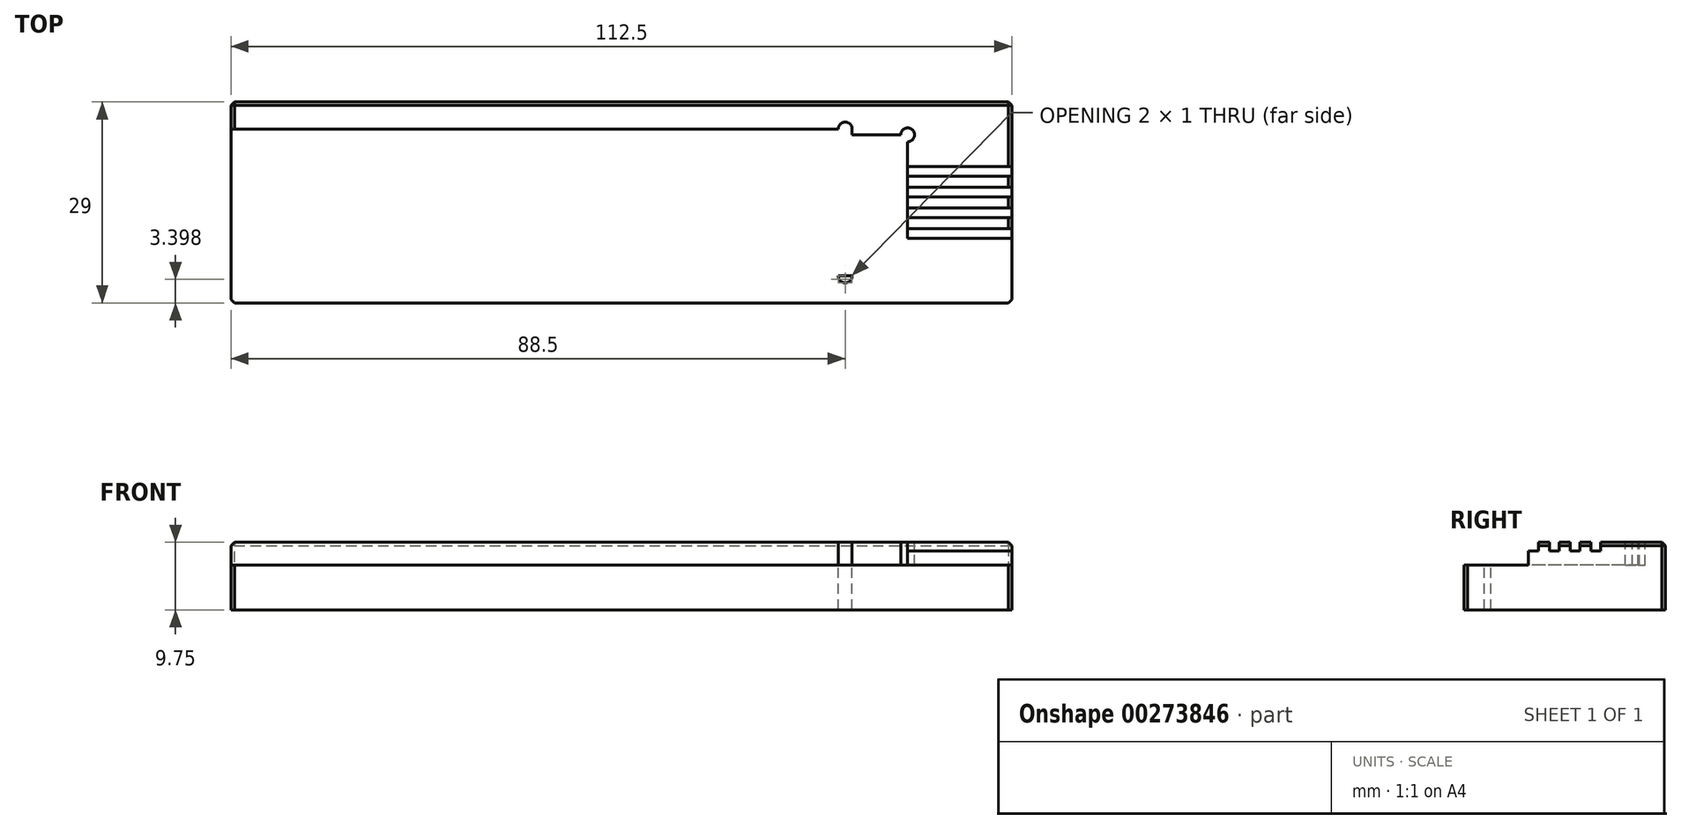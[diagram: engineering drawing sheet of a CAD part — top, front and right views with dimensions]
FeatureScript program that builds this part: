
annotation { "Feature Type Name" : "Feature", "Feature Type Description" : "" }
export const myFeature = defineFeature(function(context is Context, id is Id, definition is map)
    precondition{}
    {
        {
            var Q0;
            Q0=qCreatedBy(makeId("Top.planeOp"),FACE);
            var sketch = newSketch(context, id + "F0", { "sketchPlane" : qUnion([Q0])});
            skLineSegment(sketch, "E0.bottom", {"start": v(-42.98, 19.05) * mm, "end": v(69.52, 19.05) * mm});
            skLineSegment(sketch, "E0.top", {"start": v(-42.98, -9.95) * mm, "end": v(69.52, -9.95) * mm});
            skLineSegment(sketch, "E0.left", {"start": v(-42.98, 19.05) * mm, "end": v(-42.98, -9.95) * mm});
            skLineSegment(sketch, "E0.right", {"start": v(69.52, 19.05) * mm, "end": v(69.52, -9.95) * mm});
            skLineSegment(sketch, "E1", {"start": v(-42.98, 4.55) * mm, "end": v(114.85, 4.55) * mm, "construction": true});
            skLineSegment(sketch, "E2", {"start": v(-42.98, 15.15) * mm, "end": v(46.52, 15.15) * mm});
            skLineSegment(sketch, "E3", {"start": v(46.52, 15.15) * mm, "end": v(46.52, 4.55) * mm, "construction": true});
            skLineSegment(sketch, "E4.MirrorCS", {"start": v(-42.98, -6.05) * mm, "end": v(46.52, -6.05) * mm});
            skLineSegment(sketch, "E5.MirrorCS", {"start": v(46.52, -6.05) * mm, "end": v(46.52, 4.55) * mm, "construction": true});
            skLineSegment(sketch, "E6", {"start": v(46.52, 14.3) * mm, "end": v(54.52, 14.3) * mm});
            skLineSegment(sketch, "E7.MirrorCS", {"start": v(46.52, -5.2) * mm, "end": v(54.52, -5.2) * mm});
            skLineSegment(sketch, "E8", {"start": v(46.52, 15.15) * mm, "end": v(46.52, 14.3) * mm});
            skLineSegment(sketch, "E9", {"start": v(46.52, -5.2) * mm, "end": v(46.52, -6.05) * mm});
            skLineSegment(sketch, "E10", {"start": v(54.52, 14.3) * mm, "end": v(54.52, -5.2) * mm});
            skLineSegment(sketch, "E11.bottom", {"start": v(54.52, 5.35) * mm, "end": v(69.52, 5.35) * mm});
            skLineSegment(sketch, "E11.top", {"start": v(54.52, 6.75) * mm, "end": v(69.52, 6.75) * mm});
            skLineSegment(sketch, "E11.left", {"start": v(54.52, 5.35) * mm, "end": v(54.52, 6.75) * mm});
            skLineSegment(sketch, "E11.right", {"start": v(69.52, 5.35) * mm, "end": v(69.52, 6.75) * mm});
            skLineSegment(sketch, "E12", {"start": v(54.52, 6.05) * mm, "end": v(69.52, 6.05) * mm, "construction": true});
            skLineSegment(sketch, "E13.bottom", {"start": v(54.52, 9.75) * mm, "end": v(69.52, 9.75) * mm});
            skLineSegment(sketch, "E13.top", {"start": v(54.52, 8.35) * mm, "end": v(69.52, 8.35) * mm});
            skLineSegment(sketch, "E13.left", {"start": v(54.52, 9.75) * mm, "end": v(54.52, 8.35) * mm});
            skLineSegment(sketch, "E13.right", {"start": v(69.52, 9.75) * mm, "end": v(69.52, 8.35) * mm});
            skLineSegment(sketch, "E14", {"start": v(54.52, 9.05) * mm, "end": v(69.52, 9.05) * mm, "construction": true});
            skLineSegment(sketch, "E15.MirrorCS", {"start": v(54.52, 3.75) * mm, "end": v(69.52, 3.75) * mm});
            skLineSegment(sketch, "E16.MirrorCS", {"start": v(54.52, 2.35) * mm, "end": v(69.52, 2.35) * mm});
            skLineSegment(sketch, "E17.MirrorCS", {"start": v(54.52, 0.75) * mm, "end": v(69.52, 0.75) * mm});
            skLineSegment(sketch, "E18.MirrorCS", {"start": v(54.52, -0.65) * mm, "end": v(69.52, -0.65) * mm});
            skCircle(sketch, "E19", {"center": v(54.52, 14.3) * mm, "radius": 1 * mm});
            skCircle(sketch, "E20", {"center": v(54.52, -5.2) * mm, "radius": 1 * mm});
            skPoint(sketch, "E21", {"position": v(45.52, 15.15) * mm});
            skArc(sketch, "E22", {"start": v(46.52, 15.15) * mm, "mid": v(45.52, 16.15) * mm, "end": v(44.52, 15.15) * mm});
            skArc(sketch, "E23.MirrorCS", {"start": v(46.52, -6.05) * mm, "mid": v(45.52, -7.05) * mm, "end": v(44.52, -6.05) * mm});
            skSolve(sketch);
        }
        {
            var Q0;
            {var subQ0=sQuery(id+"F0.wireOp",EDGE,"E15.MirrorCS");Q0=makeQuery(id+"F0.imprint","IMPRINT",FACE,{"disambiguationData":[TD([[makeQuery(id+"F0.imprint","IMPRINT",EDGE,{"derivedFrom":subQ0}),-1.0]])]});}
            var Q1;
            Q1=makeQuery(id+"F0.imprint","IMPRINT",FACE,{"disambiguationData":[TD([[makeQuery(id+"F0.imprint","IMPRINT",EDGE,{"derivedFrom":sQuery(id+"F0.wireOp",EDGE,"E11.bottom")}),1.0]])]});
            var Q2;
            {var subQ0=sQuery(id+"F0.wireOp",EDGE,"E17.MirrorCS");Q2=makeQuery(id+"F0.imprint","IMPRINT",FACE,{"disambiguationData":[TD([[makeQuery(id+"F0.imprint","IMPRINT",EDGE,{"derivedFrom":subQ0}),-1.0]])]});}
            var Q3;
            Q3=makeQuery(id+"F0.imprint","IMPRINT",FACE,{"disambiguationData":[TD([[makeQuery(id+"F0.imprint","IMPRINT",EDGE,{"derivedFrom":sQuery(id+"F0.wireOp",EDGE,"E13.bottom")}),-1.0]])]});
            var Q4;
            {var subQ0=sQuery(id+"F0.wireOp",EDGE,"E11.bottom");Q4=makeQuery(id+"F0.imprint","IMPRINT",FACE,{"disambiguationData":[TD([[makeQuery(id+"F0.imprint","IMPRINT",EDGE,{"derivedFrom":subQ0}),-1.0]])]});}
            var Q5;
            {var subQ0=sQuery(id+"F0.wireOp",EDGE,"E16.MirrorCS");Q5=makeQuery(id+"F0.imprint","IMPRINT",FACE,{"disambiguationData":[TD([[makeQuery(id+"F0.imprint","IMPRINT",EDGE,{"derivedFrom":subQ0}),-1.0]])]});}
            var Q6;
            {var subQ0=sQuery(id+"F0.wireOp",EDGE,"E11.top");Q6=makeQuery(id+"F0.imprint","IMPRINT",FACE,{"disambiguationData":[TD([[makeQuery(id+"F0.imprint","IMPRINT",EDGE,{"derivedFrom":subQ0}),1.0]])]});}
            var Q7;
            {var subQ12=sQuery(id+"F0.wireOp",EDGE,"E8");Q7=makeQuery(id+"F0.imprint","IMPRINT",FACE,{"disambiguationData":[TD([[makeQuery(id+"F0.imprint","IMPRINT",EDGE,{"derivedFrom":subQ12}),-1.0]])]});}
            var Q8;
            {var subQ0=sQuery(id+"F0.wireOp",EDGE,"E23.MirrorCS");Q8=makeQuery(id+"F0.imprint","IMPRINT",FACE,{"disambiguationData":[TD([[makeQuery(id+"F0.imprint","IMPRINT",EDGE,{"derivedFrom":subQ0}),-1.0]])]});}
            var Q9;
            {var subQ0=sQuery(id+"F0.wireOp",EDGE,"E22");Q9=makeQuery(id+"F0.imprint","IMPRINT",FACE,{"disambiguationData":[TD([[makeQuery(id+"F0.imprint","IMPRINT",EDGE,{"derivedFrom":subQ0}),1.0]])]});}
            var Q10;
            {var subQ5=sQuery(id+"F0.wireOp",EDGE,"E0.bottom");Q10=makeQuery(id+"F0.imprint","IMPRINT",FACE,{"disambiguationData":[TD([[makeQuery(id+"F0.imprint","IMPRINT",EDGE,{"derivedFrom":subQ5}),-1.0]])]});}
            var Q11;
            {var subQ9=sQuery(id+"F0.wireOp",EDGE,"E0.top");Q11=makeQuery(id+"F0.imprint","IMPRINT",FACE,{"disambiguationData":[TD([[makeQuery(id+"F0.imprint","IMPRINT",EDGE,{"derivedFrom":subQ9}),1.0]])]});}
            var Q12;
            {var subQ0=sQuery(id+"F0.wireOp",EDGE,"E10");var subQ1=sQuery(id+"F0.wireOp",EDGE,"E7.MirrorCS");var subQ2=makeQuery(id+"F0.imprint","INTERSECT",VERTEX,{"derivedFrom":[subQ1,subQ0]});Q12=makeQuery(id+"F0.imprint","IMPRINT",FACE,{"disambiguationData":[TD([[makeQuery(id+"F0.imprint","IMPRINT",EDGE,{"disambiguationData":[TD([[subQ2,1.0]])],"derivedFrom":subQ1}),-1.0]])]});}
            var Q13;
            {var subQ0=sQuery(id+"F0.wireOp",EDGE,"E10");var subQ1=sQuery(id+"F0.wireOp",EDGE,"E7.MirrorCS");var subQ2=makeQuery(id+"F0.imprint","INTERSECT",VERTEX,{"derivedFrom":[subQ1,subQ0]});Q13=makeQuery(id+"F0.imprint","IMPRINT",FACE,{"disambiguationData":[TD([[makeQuery(id+"F0.imprint","IMPRINT",EDGE,{"disambiguationData":[TD([[subQ2,1.0]])],"derivedFrom":subQ1}),1.0]])]});}
            var Q14;
            {var subQ0=sQuery(id+"F0.wireOp",EDGE,"E10");var subQ1=sQuery(id+"F0.wireOp",EDGE,"E6");var subQ2=makeQuery(id+"F0.imprint","INTERSECT",VERTEX,{"derivedFrom":[subQ1,subQ0]});Q14=makeQuery(id+"F0.imprint","IMPRINT",FACE,{"disambiguationData":[TD([[makeQuery(id+"F0.imprint","IMPRINT",EDGE,{"disambiguationData":[TD([[subQ2,1.0]])],"derivedFrom":subQ1}),1.0]])]});}
            var Q15;
            {var subQ0=sQuery(id+"F0.wireOp",EDGE,"E10");var subQ1=sQuery(id+"F0.wireOp",EDGE,"E6");var subQ2=makeQuery(id+"F0.imprint","INTERSECT",VERTEX,{"derivedFrom":[subQ1,subQ0]});Q15=makeQuery(id+"F0.imprint","IMPRINT",FACE,{"disambiguationData":[TD([[makeQuery(id+"F0.imprint","IMPRINT",EDGE,{"disambiguationData":[TD([[subQ2,1.0]])],"derivedFrom":subQ1}),-1.0]])]});}
            extrude(context, id + "F1", {"entities" : qUnion([Q0, Q1, Q2, Q3, Q4, Q5, Q6, Q7, Q8, Q9, Q10, Q11, Q12, Q13, Q14, Q15]), "oppositeDirection" : true, "depth" : 9.75 * mm});
        }
        {
            var Q0;
            Q0=makeQuery(id+"F1.opExtrude","CAP_FACE",FACE,{"disambiguationData":[OSD([sQuery(id+"F0.wireOp",EDGE,"E0.bottom"),sQuery(id+"F0.wireOp",EDGE,"E0.top"),sQuery(id+"F0.wireOp",EDGE,"E0.left"),sQuery(id+"F0.wireOp",EDGE,"E0.right"),sQuery(id+"F0.wireOp",EDGE,"E11.right"),sQuery(id+"F0.wireOp",EDGE,"E13.right")])],"isStart":true});
            var Q1;
            Q1=makeQuery(id+"F1.opExtrude","SWEPT_EDGE",EDGE,{"disambiguationData":[OSD([sQuery(id+"F0.wireOp",EDGE,"E0.bottom"),sQuery(id+"F0.wireOp",EDGE,"E0.left")])]});
            var Q2;
            Q2=makeQuery(id+"F1.opExtrude","SWEPT_EDGE",EDGE,{"disambiguationData":[OSD([sQuery(id+"F0.wireOp",EDGE,"E0.top"),sQuery(id+"F0.wireOp",EDGE,"E0.left")])]});
            var Q3;
            Q3=makeQuery(id+"F1.opExtrude","SWEPT_EDGE",EDGE,{"disambiguationData":[OSD([sQuery(id+"F0.wireOp",EDGE,"E0.bottom"),sQuery(id+"F0.wireOp",EDGE,"E0.right")])]});
            var Q4;
            Q4=makeQuery(id+"F1.opExtrude","SWEPT_EDGE",EDGE,{"disambiguationData":[OSD([sQuery(id+"F0.wireOp",EDGE,"E0.top"),sQuery(id+"F0.wireOp",EDGE,"E0.right")])]});
            chamfer(context, id + "F2", {"entities" : qUnion([Q0, Q1, Q2, Q3, Q4]), "width" : 0.5 * mm, "tangentPropagation" : true});
        }
        {
            var Q0;
            {var subQ12=sQuery(id+"F0.wireOp",EDGE,"E8");Q0=makeQuery(id+"F0.imprint","IMPRINT",FACE,{"disambiguationData":[TD([[makeQuery(id+"F0.imprint","IMPRINT",EDGE,{"derivedFrom":subQ12}),-1.0]])]});}
            var Q1;
            {var subQ0=sQuery(id+"F0.wireOp",EDGE,"E23.MirrorCS");Q1=makeQuery(id+"F0.imprint","IMPRINT",FACE,{"disambiguationData":[TD([[makeQuery(id+"F0.imprint","IMPRINT",EDGE,{"derivedFrom":subQ0}),-1.0]])]});}
            var Q2;
            {var subQ0=sQuery(id+"F0.wireOp",EDGE,"E10");var subQ1=sQuery(id+"F0.wireOp",EDGE,"E7.MirrorCS");var subQ2=makeQuery(id+"F0.imprint","INTERSECT",VERTEX,{"derivedFrom":[subQ1,subQ0]});Q2=makeQuery(id+"F0.imprint","IMPRINT",FACE,{"disambiguationData":[TD([[makeQuery(id+"F0.imprint","IMPRINT",EDGE,{"disambiguationData":[TD([[subQ2,1.0]])],"derivedFrom":subQ1}),1.0]])]});}
            var Q3;
            {var subQ0=sQuery(id+"F0.wireOp",EDGE,"E10");var subQ1=sQuery(id+"F0.wireOp",EDGE,"E7.MirrorCS");var subQ2=makeQuery(id+"F0.imprint","INTERSECT",VERTEX,{"derivedFrom":[subQ1,subQ0]});Q3=makeQuery(id+"F0.imprint","IMPRINT",FACE,{"disambiguationData":[TD([[makeQuery(id+"F0.imprint","IMPRINT",EDGE,{"disambiguationData":[TD([[subQ2,1.0]])],"derivedFrom":subQ1}),-1.0]])]});}
            var Q4;
            {var subQ0=sQuery(id+"F0.wireOp",EDGE,"E10");var subQ1=sQuery(id+"F0.wireOp",EDGE,"E6");var subQ2=makeQuery(id+"F0.imprint","INTERSECT",VERTEX,{"derivedFrom":[subQ1,subQ0]});Q4=makeQuery(id+"F0.imprint","IMPRINT",FACE,{"disambiguationData":[TD([[makeQuery(id+"F0.imprint","IMPRINT",EDGE,{"disambiguationData":[TD([[subQ2,1.0]])],"derivedFrom":subQ1}),-1.0]])]});}
            var Q5;
            {var subQ0=sQuery(id+"F0.wireOp",EDGE,"E10");var subQ1=sQuery(id+"F0.wireOp",EDGE,"E6");var subQ2=makeQuery(id+"F0.imprint","INTERSECT",VERTEX,{"derivedFrom":[subQ1,subQ0]});Q5=makeQuery(id+"F0.imprint","IMPRINT",FACE,{"disambiguationData":[TD([[makeQuery(id+"F0.imprint","IMPRINT",EDGE,{"disambiguationData":[TD([[subQ2,1.0]])],"derivedFrom":subQ1}),1.0]])]});}
            var Q6;
            {var subQ0=sQuery(id+"F0.wireOp",EDGE,"E22");Q6=makeQuery(id+"F0.imprint","IMPRINT",FACE,{"disambiguationData":[TD([[makeQuery(id+"F0.imprint","IMPRINT",EDGE,{"derivedFrom":subQ0}),1.0]])]});}
            extrude(context, id + "F3", {"entities" : qUnion([Q0, Q1, Q2, Q3, Q4, Q5, Q6]), "operationType" : NewBodyOperationType.REMOVE, "oppositeDirection" : true, "depth" : 3.32 * mm});
        }
        {
            var Q0;
            Q0=makeQuery(id+"F0.imprint","IMPRINT",FACE,{"disambiguationData":[TD([[makeQuery(id+"F0.imprint","IMPRINT",EDGE,{"derivedFrom":sQuery(id+"F0.wireOp",EDGE,"E13.bottom")}),-1.0]])]});
            var Q1;
            Q1=makeQuery(id+"F0.imprint","IMPRINT",FACE,{"disambiguationData":[TD([[makeQuery(id+"F0.imprint","IMPRINT",EDGE,{"derivedFrom":sQuery(id+"F0.wireOp",EDGE,"E11.bottom")}),1.0]])]});
            var Q2;
            {var subQ0=sQuery(id+"F0.wireOp",EDGE,"E15.MirrorCS");Q2=makeQuery(id+"F0.imprint","IMPRINT",FACE,{"disambiguationData":[TD([[makeQuery(id+"F0.imprint","IMPRINT",EDGE,{"derivedFrom":subQ0}),-1.0]])]});}
            var Q3;
            {var subQ0=sQuery(id+"F0.wireOp",EDGE,"E17.MirrorCS");Q3=makeQuery(id+"F0.imprint","IMPRINT",FACE,{"disambiguationData":[TD([[makeQuery(id+"F0.imprint","IMPRINT",EDGE,{"derivedFrom":subQ0}),-1.0]])]});}
            extrude(context, id + "F4", {"entities" : qUnion([Q0, Q1, Q2, Q3]), "operationType" : NewBodyOperationType.REMOVE, "oppositeDirection" : true, "depth" : 1.25 * mm});
        }
    });
